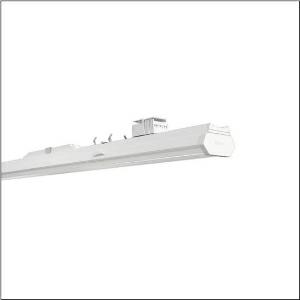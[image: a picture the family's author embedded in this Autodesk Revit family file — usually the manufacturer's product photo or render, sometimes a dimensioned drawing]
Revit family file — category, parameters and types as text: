
# Revit family: licross_r__21_dc_protected_55td1bdn495g_936f
name_source: partatom
category: Lighting Fixtures
units: mm (PartAtom-declared; Revit-internal decimal feet)

## family parameters
Cut with Voids When Loaded = No
Host = Face
Light Source = No
Part Type = Normal
Room Calculation Point = No
Round Connector Dimension = Use Diameter
Shared = No

## types (1)
- --- (1 x LED, 9650 lm, 59.1 W, 4000K)
    Apparent Load = 59 VA
    CIE Flux Codes = 54 82 95 97 100
    Color Rendering = 80
    Color Temperature = 4000K
    Default Elevation = 1800 mm
    Description = Licross® 21 DC Protected, luminaire insert, of sheet steel, galvanised, coil coated, white, length: 1.500mm, width: 90mm, height: 101mm, LED rated luminous flux: 9.650lm, light colour: 840, control gear: DALI 2, with plug, 5-pole, without phase selection, mains connection: 650V, DC, rated input power: 59W, internal wiring halogen-free, option to choose between normal mains or equivalent power supply by moving two contact pins without tools before inserting it into the trunking rail, primary optical cover: cover, of PMMA, light emission: direct distribution, primary light characteristic: symmetric, protection rating (complete): IP54, insulation class (complete): insulation class I (protective earthing), certification: CE, UKCA, protection symbol: D if used in an environment with non-conductive dust loads with corresponding accessories, impact resistance: IK06, permissible ambient temperature for indoor applications: -30..+40°C, corresponds to IFS (International Featured Standards) requirements for safety and quality in the food industry, reducing of maximum allowable ambient temperature of 5°C with ceiling mounting, LABS conformity tested according to VDMA 24364:2018-05, packaging unit: 1 piece
    Height = 92 mm
    Lamp = 1 x LED
    Lamp Light Flux = 9650 lm
    Lamp Power = 59.1 W
    Lamp count = 1
    Length = 1500 mm
    Luminous efficacy = 163 lm/W
    Manufacturer = Siteco
    ModVariant = No
    Model = 55TD1BDN495G
    Mounting Place = Ceiling
    Mounting Type = Pendant
    Number of Poles = 1
    OnlyDefault = Yes
    Power Factor = 1
    Product Name = Licross® 21 DC Protected
    Product group = luminaire insert | ceiling pendant
    ProductGroupID = 902
    Protection Class = Protection class I
    Protection Degree = IP 54
    RLX_Detail_Level = 1
    RLX_Emergency_Light_Flux = 0 lm
    RLX_Emergency_Type = 0
    RLX_Emergency_Type_DB = No
    RlxData = <blob elided: 24613 chars, md5=84f69102>
    Socket = socket
    Standby Power = 0 W
    System Light Flux = 9650 lm
    System Power = 59 W
    Type Comments = factory setting: luminous flux: 100 % | dim-lin: 254 | 400 mA
    Type Image = l_1256148.jpg
    URL = http://relux.com
    VarID = @adj_004183
    Voltage = 0 V
    Weight = 0.00 kg
    Width = 88 mm

## geometry (parser evidence)
native form markers: Blend x4, Sweep x8
no freeform markers — native parametric forms only
